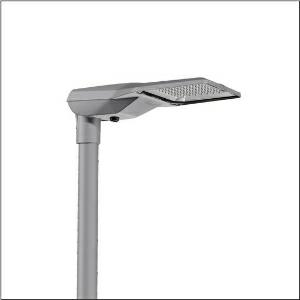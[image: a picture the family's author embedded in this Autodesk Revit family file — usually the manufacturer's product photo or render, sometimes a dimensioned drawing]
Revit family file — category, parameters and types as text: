
# Revit family: streetlight_sl_21_midi___p0_8a_5xe3u33r08lb_5b19
name_source: partatom
category: Lighting Fixtures
units: mm (PartAtom-declared; Revit-internal decimal feet)

## family parameters
Cut with Voids When Loaded = No
Host = Face
Light Source = No
Part Type = Normal
Room Calculation Point = No
Round Connector Dimension = Use Diameter
Shared = No

## types (1)
- --- (1 x LED, 14470 lm, 99.6 W, 3000K)
    Apparent Load = 100 VA
    CIE Flux Codes = 33 69 96 100 100
    Color Rendering = 70
    Color Temperature = 3000K
    Default Elevation = 1800 mm
    Description = Streetlight SL 21 midi, mast luminaire, primary light control with lens, of PMMA, primary optical cover: cover, of toughened safety glass, transparent, light distribution: P0.8a, light emission: direct distribution, primary light characteristic: asymmetric, installation type: post-top, side-entry, LED, High Power LED, rated luminous flux: 14.470lm, luminous efficacy: 145lm/W, light colour: 730, colour temperature: 3000K, control gear: D4i, control: pre-setting: logarithmic dimming characteristic, flexible luminous flux parameterisation, time-dependent luminous flux control, constant luminous flux control, overheat protection, mains connection: 230..240V, AC, 50/60Hz, start of lifetime: 100W, end of service life: 102W, reduction: 46W, luminaire housing, of diecast aluminium, powder-coated, Siteco® metallic grey (DB 702S), corrosivity category C5 mid according to DIN EN ISO 12944, multi-level sealing system, sealing non-destructively replaceable, inclination adjustable: 0°, 5°, 10°, 15°, please order mast flange separately, length: 644mm, width: 335mm, height: 110mm, mast flange for spigot size: 42mm (side-entry): 5XC10008XM4, 60/48mm (side-entry/post-top): 5XC10108XM2, 76/60mm (side-entry/post-top): 5XC10108XM1, mounting height: 4..8m, Smart Interface below, protection rating (complete): IP66, insulation class (complete): insulation class II (safety insulation), certification: CE, ENEC, ENEC+, VDE, impact resistance: IK10, permissible operating ambient temperature for outdoor applications: -40..+50°C, standard-compliant lighting for roads and squares, packaging unit: 1 piece

Light Distribution: P0.8a
    Height = 111 mm
    Lamp = 1 x LED
    Lamp Light Flux = 14470 lm
    Lamp Power = 99.6 W
    Lamp count = 1
    Length = 644 mm
    Luminous efficacy = 145 lm/W
    Manufacturer = Siteco
    ModVariant = No
    Model = 5XE3U33R08LB
    Number of Poles = 1
    OnlyDefault = Yes
    Power Factor = 1
    Product Name = Streetlight SL 21 midi | P0.8a
    Product group = mast luminaire | pylon top
    ProductGroupID = 6100
    Protection Class = Protection class II
    Protection Degree = IP 66
    RLX_Detail_Level = 1
    RLX_Emergency_Light_Flux = 0 lm
    RLX_Emergency_Type = 0
    RLX_Emergency_Type_DB = No
    RlxData = <blob elided: 26697 chars, md5=b7364808>
    Socket = socket
    Standby Power = 0 W
    System Light Flux = 14470 lm
    System Power = 100 W
    Type Comments = factory setting: luminous flux: 100 % | dim-lin: 254 | 1020 mA
    Type Image = l_1004300.jpg
    URL = http://relux.com
    VarID = @adj_033471
    Voltage = 0 V
    Weight = 0.00 kg
    Width = 336 mm

## geometry (parser evidence)
native form markers: Blend x4, Sweep x10
no freeform markers — native parametric forms only
